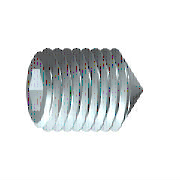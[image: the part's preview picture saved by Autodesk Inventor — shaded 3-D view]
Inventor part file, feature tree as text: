
AUTODESK INVENTOR PART (.ipt)
format: ipt  version: 2020 (Build 240168000, 168)  size: 165,376 bytes
history: native  units: mm (DEFAULTED — no unit token found)
features: sketch x2, extrude x1, other x1, plane x1
ambient origin geometry x8: Origin, YZ Plane, XZ Plane, XY Plane, X Axis, Y Axis, Z Axis, Center Point
bodies: Solid1 (feature_tree), Body (feature_tree)
feature tree (5):
  extrude  "Slot"  TaperAngle=60.0deg  [1 undecoded]
  other  "Work Axis1"
  plane  "Work Plane1"
  sketch  "Sketch1"  dims[d0=3.0mm d1=60.0deg]
  sketch  "Sketch2"  dims[d2=5.0mm d3=2.886751mm d6=90.0deg d4=0.0mm d5=10.0mm d21=10.0mm d7=0.0mm d8=2.499995mm d9=45.0deg d10=0.49076mm d11=45.0deg d12=10.0mm d13=0.0mm d34=2.499995mm d35=0.49076mm d36=0.0mm d37=0.0mm]
note: 1 required parameter value undecoded (feature->parameter linkage not recoverable at this tier; creation-order binding heuristic only, values carry confidence <= 0.55)
